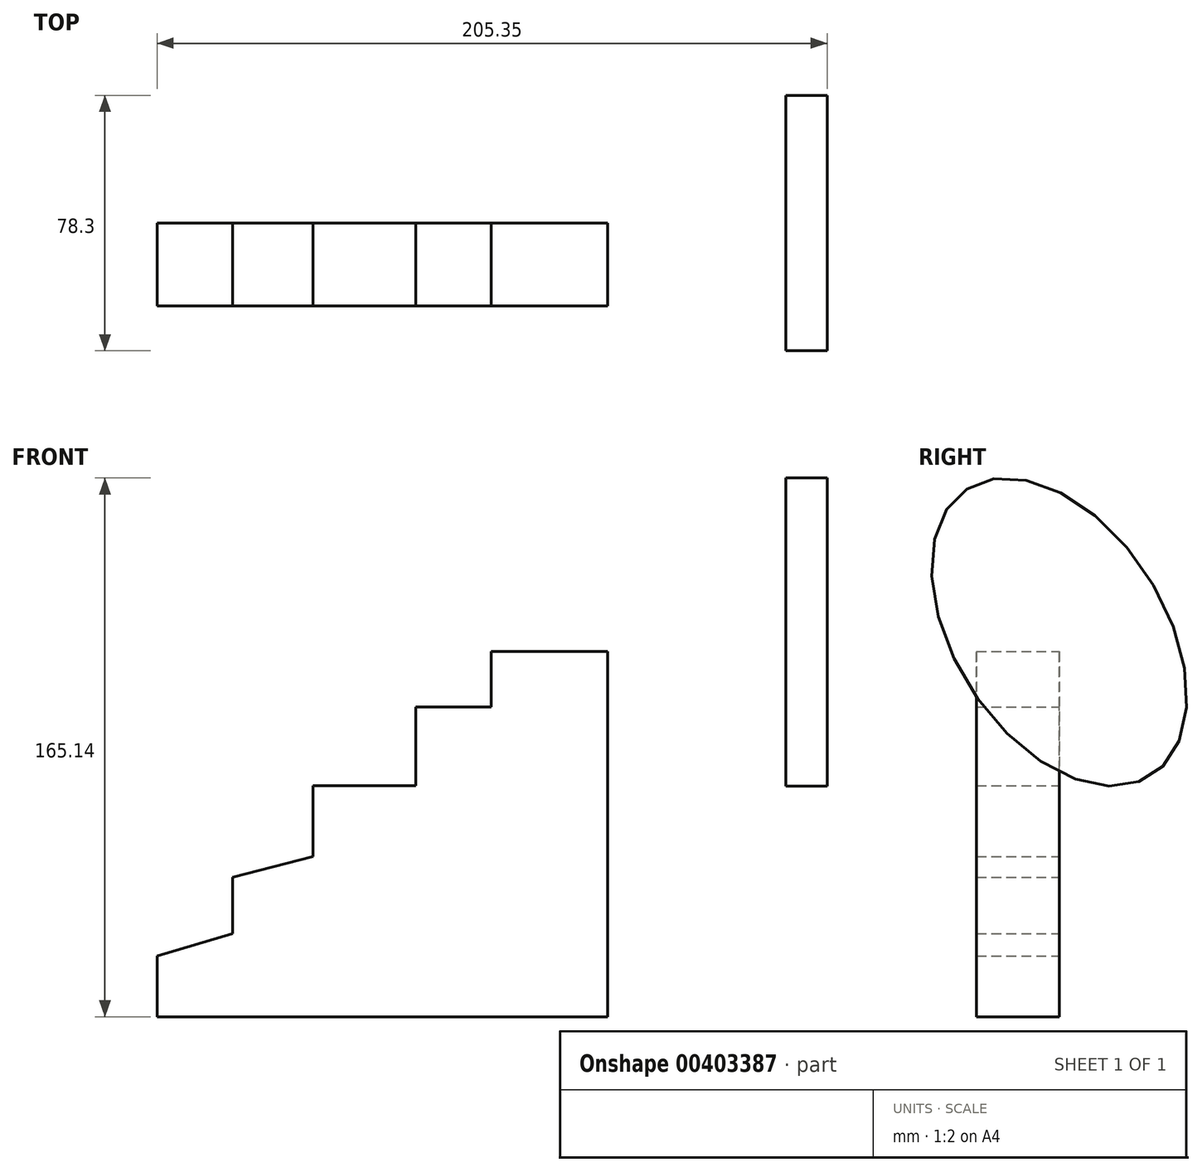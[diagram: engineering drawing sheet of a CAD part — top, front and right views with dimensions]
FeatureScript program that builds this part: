
annotation { "Feature Type Name" : "Feature", "Feature Type Description" : "" }
export const myFeature = defineFeature(function(context is Context, id is Id, definition is map)
    precondition{}
    {
        {
            var Q0;
            Q0=qCreatedBy(makeId("Right.planeOp"),FACE);
            var sketch = newSketch(context, id + "F0", { "sketchPlane" : qUnion([Q0])});
            skEllipse(sketch, "E0", {"center": v(0, 0) * mm, "majorRadius": 52.26 * mm, "minorRadius": 32.14 * mm, "majorAxis": v(-0.54, 0.84)});
            skSolve(sketch);
        }
        {
            var Q0;
            Q0 = qSketchRegion(id + "F0", true);
            extrude(context, id + "F1", {"entities" : qUnion([Q0]), "depth" : 12.7 * mm});
        }
        {
            var Q0;
            Q0 = qSketchRegion(id + "F0", true);
            extrude(context, id + "F2", {"entities" : qUnion([Q0]), "operationType" : NewBodyOperationType.ADD, "depth" : 7.62 * mm});
        }
        {
            var Q0;
            Q0=qCreatedBy(makeId("Front.planeOp"),FACE);
            var sketch = newSketch(context, id + "F3", { "sketchPlane" : qUnion([Q0])});
            skLineSegment(sketch, "E1", {"start": v(-192.65, -117.9) * mm, "end": v(-192.65, -99.28) * mm});
            skLineSegment(sketch, "E2", {"start": v(-192.65, -99.28) * mm, "end": v(-169.47, -92.38) * mm});
            skLineSegment(sketch, "E3", {"start": v(-169.47, -92.38) * mm, "end": v(-169.47, -75.2) * mm});
            skLineSegment(sketch, "E4", {"start": v(-169.47, -75.2) * mm, "end": v(-144.85, -68.76) * mm});
            skLineSegment(sketch, "E5", {"start": v(-144.85, -68.76) * mm, "end": v(-144.85, -47.04) * mm});
            skLineSegment(sketch, "E6", {"start": v(-144.85, -47.04) * mm, "end": v(-113.3, -47.04) * mm});
            skLineSegment(sketch, "E7", {"start": v(-113.3, -47.04) * mm, "end": v(-113.3, -23) * mm});
            skLineSegment(sketch, "E8", {"start": v(-113.3, -23) * mm, "end": v(-90.22, -23) * mm});
            skLineSegment(sketch, "E9", {"start": v(-90.22, -23) * mm, "end": v(-90.22, -5.95) * mm});
            skLineSegment(sketch, "E10", {"start": v(-90.22, -5.95) * mm, "end": v(-54.6, -5.95) * mm});
            skLineSegment(sketch, "E11", {"start": v(-54.6, -5.95) * mm, "end": v(-54.6, -117.9) * mm});
            skLineSegment(sketch, "E12", {"start": v(-54.6, -117.9) * mm, "end": v(-192.65, -117.9) * mm});
            skSolve(sketch);
        }
        {
            var Q0;
            Q0 = qSketchRegion(id + "F3", true);
            extrude(context, id + "F4", {"entities" : qUnion([Q0]), "depth" : 25.4 * mm});
        }
    });
